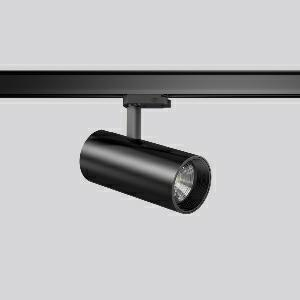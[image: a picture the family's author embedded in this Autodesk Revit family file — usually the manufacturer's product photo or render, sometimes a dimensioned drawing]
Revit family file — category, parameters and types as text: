
# Revit family: deecos_s_mini_742199_003_1_0318
name_source: partatom
category: Lighting Fixtures
units: mm (PartAtom-declared; Revit-internal decimal feet)

## family parameters
Cut with Voids When Loaded = No
Host = Face
Light Source = No
Part Type = Normal
Room Calculation Point = No
Round Connector Dimension = Use Diameter
Shared = No

## types (1)
- DEECOS S mini (1 x LED Modul 940, 2250 lm, 4000)
    Apparent Load = 20 VA
    Approval mark = CE
    CIE Flux Codes = 96 100 100 100 100
    Color Rendering = 92
    Color Temperature = 4000
    Default Elevation = 1800 mm
    Description = Series: DEECOS S mini
LED surface-mounted projector in modern design with no visible cooling ribs. Housing: die-cast aluminium, powder-coated. Rotation range: 356°. Swivel range: 90°. Black plastic ring and recessed LED to prevent glare from the side. Optical assembly with lens made of plastic (polycarbonate) for the best homogeneous light distribution - can be changed without tools. Best colour rendering index Ra>90. With multi adaptor for 3-circuit tracks 230 V. Suitable for Track on ceiling, Wall track. High quality converter without flickering and stroboscopic effect. The following accessories can be mounted without use of tools: interchangeable lenses, decorative glasses, honeycomb louvre, clear and frosted diffusers, white interchangeable plastic ring. 
Colour: deep black, matt (RAL 9005)
Diameter: 87 mm
Height: 214 mm
Lamp: LED
Socket: without socket
Colour temperature: 4000K
Colour rendering index (CRI): 92
System power: 20 W
Rated luminous flux: 2250 lm
Luminous efficiency: 113 lm/W
Control gear: Regulated power supply
Protection class: I
Type of protection: IP 20
    Height = 214 mm
    Lamp = 1 x LED Modul 940
    Lamp Light Flux = 2250 lm
    Lamp count = 1
    Length = 87 mm
    Lifetime = 50000 h
    Luminous efficacy = 113 lm/W
    Manufacturer = RZB
    ModVariant = No
    Model = 742199.003.1
    Mounting Place = Ceiling
    Mounting Type = Rail mounted
    Number of Poles = 1
    OnlyDefault = Yes
    Power Factor = 1
    Product Name = DEECOS S mini
    Product group = Track mounted projectors
    ProductGroupID = 301
    Protection Class = Protection class I
    Protection Degree = IP 20
    RLX_Detail_Level = 1
    RLX_Emergency_Light_Flux = 0 lm
    RLX_Emergency_Type = 0
    RLX_Emergency_Type_DB = No
    RlxData = <blob elided: 38933 chars, md5=63616436>
    Socket = socket
    Standby Power = 0 W
    System Light Flux = 2250 lm
    System Power = 20 W
    Type Comments = Product without accessories
    Type Image = 741930.003.jpg
    URL = http://relux.com
    VarID = ---
    Voltage = 230 V
    Voltage Range = 220-240 V
    Weight = 0.00 kg
    Width = 0 mm  [stored 0 ft]

note: [stored X ft] marks values corroborated as IEEE doubles in the binary element streams (Revit-internal decimal feet)

## geometry (parser evidence)
native form markers: Blend x4, Sweep x11
no freeform markers — native parametric forms only
